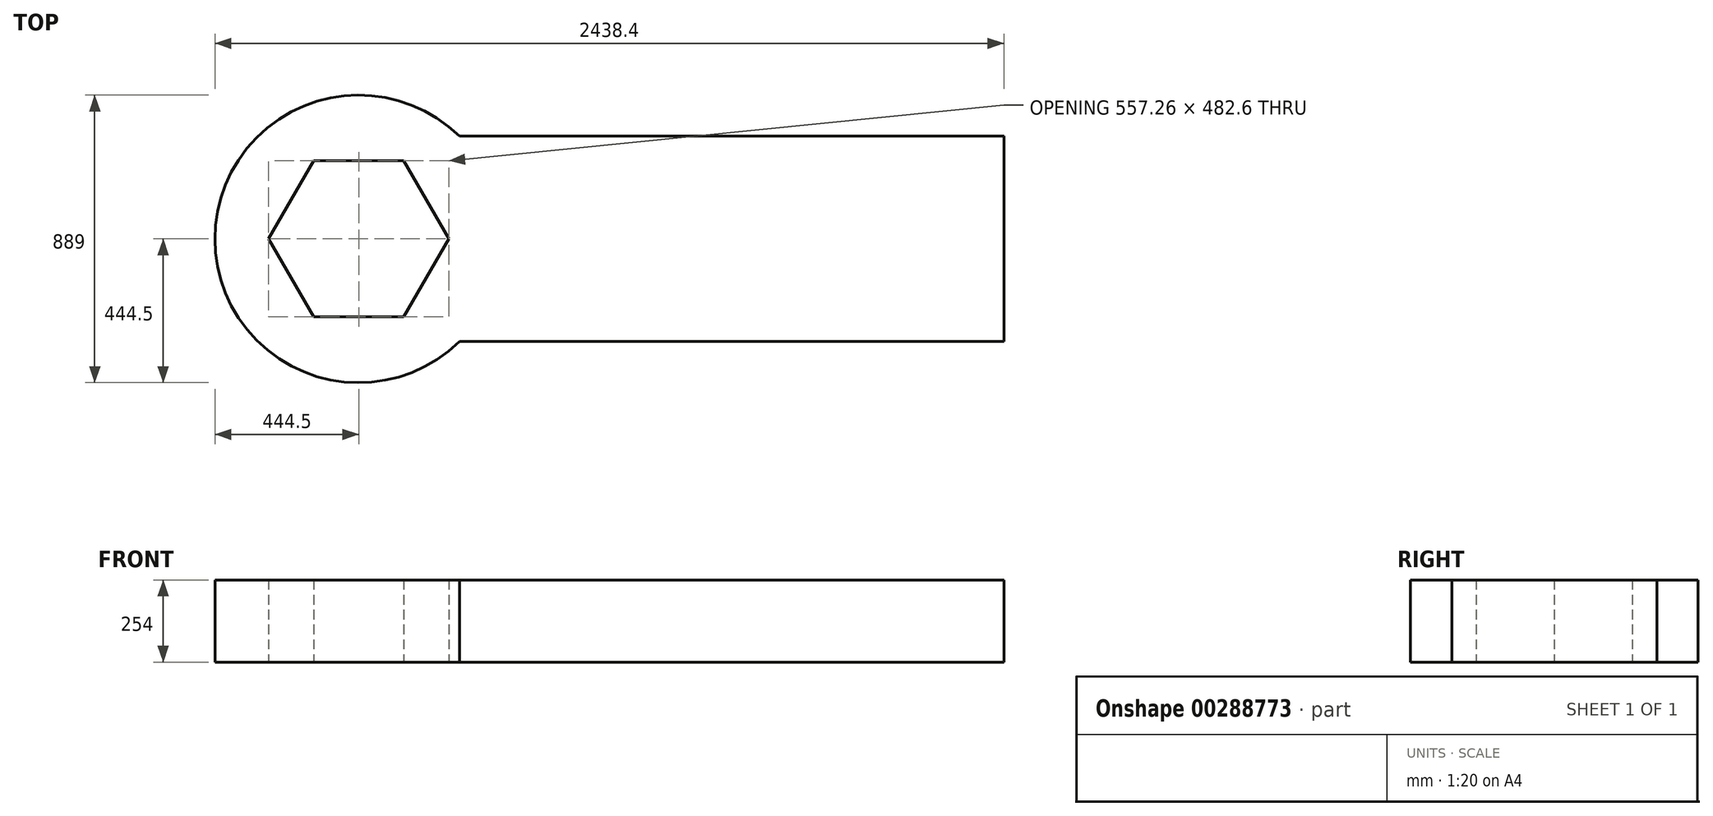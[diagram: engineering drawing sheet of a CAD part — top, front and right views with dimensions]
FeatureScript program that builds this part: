
annotation { "Feature Type Name" : "Feature", "Feature Type Description" : "" }
export const myFeature = defineFeature(function(context is Context, id is Id, definition is map)
    precondition{}
    {
        {
            var Q0;
            Q0=qCreatedBy(makeId("Top.planeOp"),FACE);
            var sketch = newSketch(context, id + "F0", { "sketchPlane" : qUnion([Q0])});
            skCircle(sketch, "E0", {"center": v(-736.6, 0) * mm, "radius": 444.5 * mm});
            skLineSegment(sketch, "E1", {"start": v(0, 317.5) * mm, "end": v(0, -317) * mm});
            skLineSegment(sketch, "E2", {"start": v(0, 317.5) * mm, "end": v(-425.51, 317.5) * mm});
            skLineSegment(sketch, "E3", {"start": v(0, -317) * mm, "end": v(-425.01, -317) * mm});
            skCircle(sketch, "E4.cCircle", {"center": v(-736.6, 0) * mm, "radius": 241.3 * mm, "construction": true});
            skLineSegment(sketch, "E4.0", {"start": v(-597.29, 241.3) * mm, "end": v(-457.97, 0) * mm});
            skLineSegment(sketch, "E4.1", {"start": v(-457.97, 0) * mm, "end": v(-597.29, -241.3) * mm});
            skLineSegment(sketch, "E4.2", {"start": v(-597.29, -241.3) * mm, "end": v(-875.91, -241.3) * mm});
            skLineSegment(sketch, "E4.3", {"start": v(-875.91, -241.3) * mm, "end": v(-1015.23, 0) * mm});
            skLineSegment(sketch, "E4.4", {"start": v(-1015.23, 0) * mm, "end": v(-875.91, 241.3) * mm});
            skLineSegment(sketch, "E4.5", {"start": v(-875.91, 241.3) * mm, "end": v(-597.29, 241.3) * mm});
            skPoint(sketch, "E4.0.midPoint", {"position": v(-527.63, 120.65) * mm});
            skLineSegment(sketch, "E5", {"start": v(0, -317) * mm, "end": v(1257.3, -317) * mm});
            skLineSegment(sketch, "E6", {"start": v(0, 317.5) * mm, "end": v(1257.3, 317.5) * mm});
            skLineSegment(sketch, "E7", {"start": v(1257.3, -317) * mm, "end": v(1257.3, 317.5) * mm});
            skPoint(sketch, "E8.end.orphan", {"position": v(-636.48, -433.08) * mm});
            skPoint(sketch, "E9.end.orphan", {"position": v(-636.48, 433.57) * mm});
            skSolve(sketch);
        }
        {
            var Q0;
            Q0=makeQuery(id+"F0.imprint","IMPRINT",FACE,{"disambiguationData":[TD([[makeQuery(id+"F0.imprint","IMPRINT",EDGE,{"derivedFrom":sQuery(id+"F0.wireOp",EDGE,"E4.0")}),1.0]])]});
            var Q1;
            Q1=makeQuery(id+"F0.imprint","IMPRINT",FACE,{"disambiguationData":[TD([[makeQuery(id+"F0.imprint","IMPRINT",EDGE,{"derivedFrom":sQuery(id+"F0.wireOp",EDGE,"iJlgfBez-sRjN-4QWt-sn4x-tNyvCTPUL2gx")}),1.0]])]});
            var Q2;
            Q2=makeQuery(id+"F0.imprint","IMPRINT",FACE,{"disambiguationData":[TD([[makeQuery(id+"F0.imprint","IMPRINT",EDGE,{"derivedFrom":sQuery(id+"F0.wireOp",EDGE,"E1")}),1.0]])]});
            var Q3;
            Q3=makeQuery(id+"F0.imprint","IMPRINT",FACE,{"disambiguationData":[TD([[makeQuery(id+"F0.imprint","IMPRINT",EDGE,{"derivedFrom":sQuery(id+"F0.wireOp",EDGE,"E1")}),-1.0]])]});
            extrude(context, id + "F1", {"entities" : qUnion([Q0, Q1, Q2, Q3]), "depth" : 254 * mm});
        }
    });
